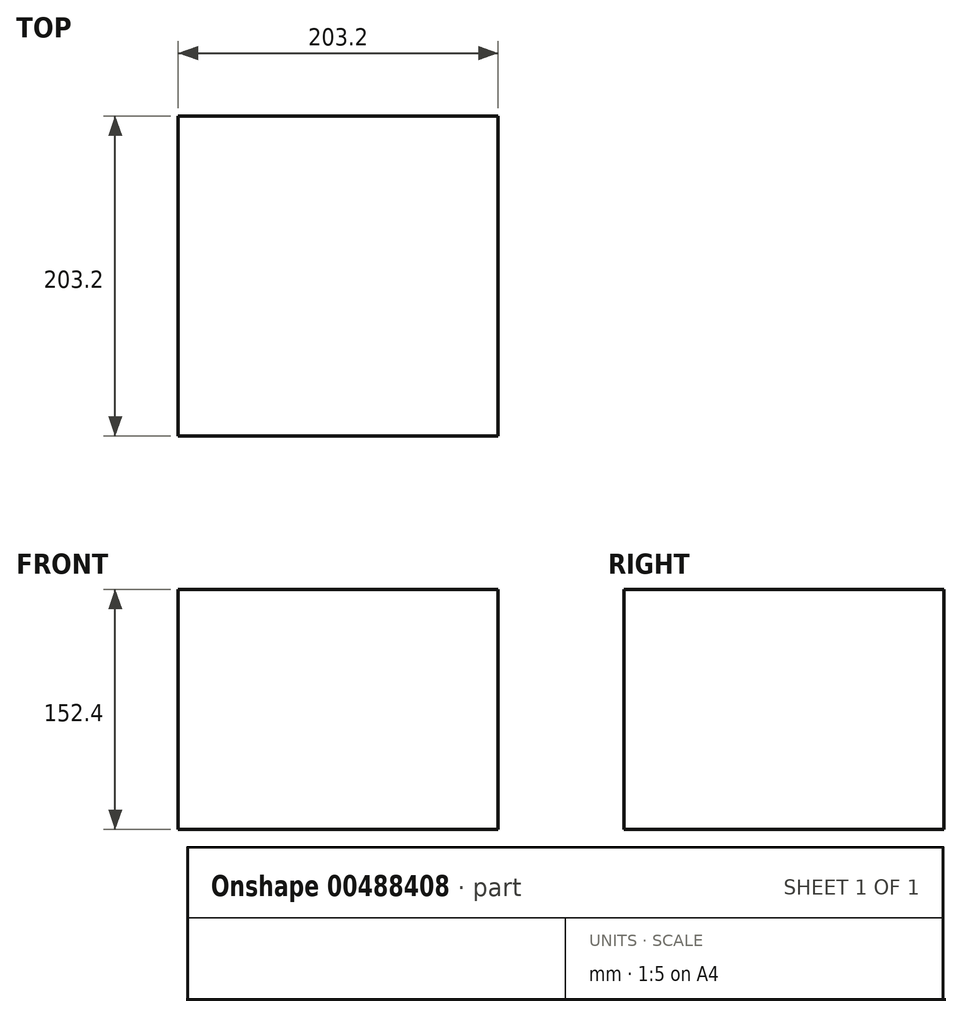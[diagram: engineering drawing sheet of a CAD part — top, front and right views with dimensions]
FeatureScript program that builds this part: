
annotation { "Feature Type Name" : "Feature", "Feature Type Description" : "" }
export const myFeature = defineFeature(function(context is Context, id is Id, definition is map)
    precondition{}
    {
        {
            var Q0;
            Q0=qCreatedBy(makeId("Top.planeOp"),FACE);
            var sketch = newSketch(context, id + "F0", { "sketchPlane" : qUnion([Q0])});
            skLineSegment(sketch, "E0.bottom", {"start": v(-101, 105.59) * mm, "end": v(102.2, 105.59) * mm});
            skLineSegment(sketch, "E0.top", {"start": v(-101, -97.61) * mm, "end": v(102.2, -97.61) * mm});
            skLineSegment(sketch, "E0.left", {"start": v(-101, 105.59) * mm, "end": v(-101, -97.61) * mm});
            skLineSegment(sketch, "E0.right", {"start": v(102.2, 105.59) * mm, "end": v(102.2, -97.61) * mm});
            skSolve(sketch);
        }
        {
            var Q0;
            Q0 = qSketchRegion(id + "F0", true);
            extrude(context, id + "F1", {"entities" : qUnion([Q0]), "depth" : 152.4 * mm});
        }
    });
